# Revit family: Moment Steel Leg Rectangular 800 Deep
name_source: partatom
category: Furniture
revit_build: Autodesk Revit 2016 (Build: 20151007_0715(x64)
units: mm (PartAtom-declared; Revit-internal decimal feet)

## family parameters
Always vertical = Yes
Cut with Voids When Loaded = No
OmniClass Number = 23.40.20.00
OmniClass Title = General Furniture and Specialties
Room Calculation Point = No
Shared = No
Work Plane-Based = No

## types (7) — shared parameters
Assembly Code = E2020200
Foot = Gresham - Black Plastic
Frame = Gresham - Silver Metal
Manufacturer = Gresham Office Furniture
Range = MOMENT
Table Top = Gresham - White MFC
URL = www.gof.co.uk

## per-type parameters (varying)
| type | Product Code | Width |
| 1400 x 800 | MSTR1408 | 1400 mm  [stored 4.59318 ft] |
| 1600 x 800 | MSTR1608 | 1600 mm  [stored 5.24934 ft] |
| 1800 x 800 | MSTR1808 | 1800 mm  [stored 5.90551 ft] |
| 1200 x 800 | MSTR1208 | 1200 mm |
| 2000 x 800 | MSTR2008 | 2000 mm  [stored 6.56168 ft] |
| 2200 x 800 | MSTR2208 | 2200 mm |
| 2400 x 800 | MSTR2408 | 2400 mm  [stored 7.87402 ft] |

note: [stored X ft] marks values corroborated as IEEE doubles in the binary element streams (Revit-internal decimal feet)

## geometry (parser evidence)
native form markers: Blend x2, Sweep x6
no freeform markers — native parametric forms only
